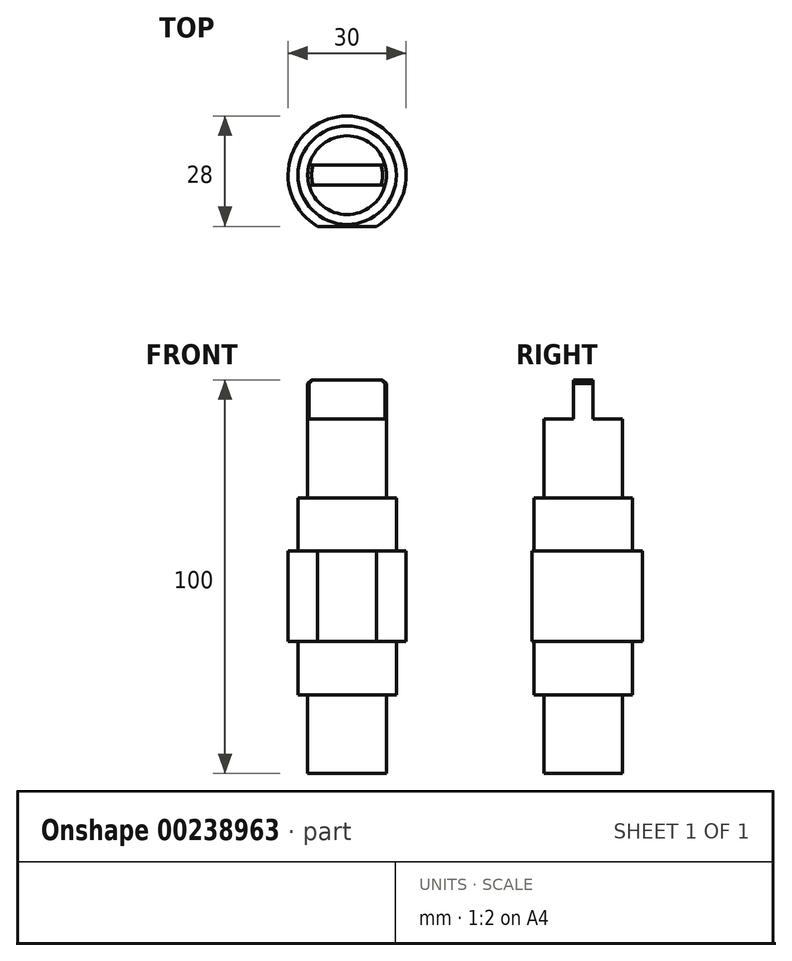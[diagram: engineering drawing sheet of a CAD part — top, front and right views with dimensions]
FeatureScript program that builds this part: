
annotation { "Feature Type Name" : "Feature", "Feature Type Description" : "" }
export const myFeature = defineFeature(function(context is Context, id is Id, definition is map)
    precondition{}
    {
        {
            var Q0;
            Q0=qCreatedBy(makeId("Front.planeOp"),FACE);
            var sketch = newSketch(context, id + "F0", { "sketchPlane" : qUnion([Q0])});
            skLineSegment(sketch, "E0", {"start": v(-15, 11.5) * mm, "end": v(-15, 0) * mm});
            skLineSegment(sketch, "E1", {"start": v(-10, 45) * mm, "end": v(0, 45) * mm});
            skLineSegment(sketch, "E2.MirrorCS", {"start": v(-15, 0) * mm, "end": v(-15, 11.5) * mm});
            skLineSegment(sketch, "E3", {"start": v(0, 45) * mm, "end": v(0, 0) * mm});
            skLineSegment(sketch, "E4", {"start": v(-15, 11.5) * mm, "end": v(-12.5, 11.5) * mm});
            skLineSegment(sketch, "E5", {"start": v(-12.5, 25) * mm, "end": v(-12.5, 11.5) * mm});
            skLineSegment(sketch, "E6", {"start": v(-12.5, 25) * mm, "end": v(-10, 25) * mm});
            skLineSegment(sketch, "E7", {"start": v(-10, 45) * mm, "end": v(-10, 25) * mm});
            skLineSegment(sketch, "E8", {"start": v(12.24, 0) * mm, "end": v(-26.8, 0) * mm, "construction": true});
            skLineSegment(sketch, "E9.MirrorCS", {"start": v(0, -45) * mm, "end": v(0, 0) * mm});
            skLineSegment(sketch, "E10.MirrorCS", {"start": v(-10, -45) * mm, "end": v(0, -45) * mm});
            skLineSegment(sketch, "E11.MirrorCS", {"start": v(-10, -45) * mm, "end": v(-10, -25) * mm});
            skLineSegment(sketch, "E12.MirrorCS", {"start": v(-12.5, -25) * mm, "end": v(-10, -25) * mm});
            skLineSegment(sketch, "E13.MirrorCS", {"start": v(-12.5, -25) * mm, "end": v(-12.5, -11.5) * mm});
            skLineSegment(sketch, "E14.MirrorCS", {"start": v(-15, -11.5) * mm, "end": v(-12.5, -11.5) * mm});
            skLineSegment(sketch, "E15.MirrorCS", {"start": v(-15, 0) * mm, "end": v(-15, -11.5) * mm});
            skSolve(sketch);
        }
        {
            var Q0;
            Q0=qSketchRegion(id+"F0",true);
            var Q1;
            Q1=sQuery(id+"F0.wireOp",EDGE,"E3");
            revolve(context, id + "F1", {"entities" : qUnion([Q0]), "axis" : qUnion([Q1]), "revolveType" : RevolveType.FULL});
        }
        {
            var Q0;
            Q0=qCreatedBy(makeId("Top.planeOp"),FACE);
            var sketch = newSketch(context, id + "F2", { "sketchPlane" : qUnion([Q0])});
            skLineSegment(sketch, "E16", {"start": v(-18, -12.5) * mm, "end": v(24.59, -12.5) * mm, "construction": true});
            skLineSegment(sketch, "E17", {"start": v(-15, -13) * mm, "end": v(0, -13) * mm});
            skLineSegment(sketch, "E18", {"start": v(-15, -17) * mm, "end": v(0, -17) * mm});
            skLineSegment(sketch, "E19.trimOffspring", {"start": v(-15, -13) * mm, "end": v(-15, -17) * mm});
            skLineSegment(sketch, "E20.MirrorCS", {"start": v(15, -13) * mm, "end": v(0, -13) * mm});
            skLineSegment(sketch, "E21.MirrorCS", {"start": v(15, -13) * mm, "end": v(15, -17) * mm});
            skLineSegment(sketch, "E22.MirrorCS", {"start": v(15, -17) * mm, "end": v(0, -17) * mm});
            skCircle(sketch, "E23.0", {"center": v(0, 0) * mm, "radius": 10 * mm, "construction": true});
            skCircle(sketch, "E24.0", {"center": v(0, 0) * mm, "radius": 12.5 * mm, "construction": true});
            skSolve(sketch);
        }
        {
            var Q0;
            Q0=qSketchRegion(id+"F2",true);
            extrude(context, id + "F3", {"entities" : qUnion([Q0]), "operationType" : NewBodyOperationType.REMOVE, "depth" : 25 * mm, "hasSecondDirection" : true, "secondDirectionOppositeDirection" : true, "secondDirectionDepth" : 25 * mm});
        }
        {
            var Q0;
            Q0=makeQuery(id+"F1.opRevolve","SWEPT_FACE",FACE,{"disambiguationData":[OSD([sQuery(id+"F0.wireOp",EDGE,"E1")])]});
            cPlane(context, id + "F4", {"entities" : qUnion([Q0]), "cplaneType" : CPlaneType.OFFSET, "offset" : 0 * mm, "width" : 150 * mm, "height" : 150 * mm});
        }
        {
            var Q0;
            Q0=qCreatedBy(id+"F4.planeOp",FACE);
            var sketch = newSketch(context, id + "F5", { "sketchPlane" : qUnion([Q0])});
            skArc(sketch, "E25.0.0", {"start": v(-9.68, 2.5) * mm, "mid": v(-10, 0) * mm, "end": v(-9.68, -2.5) * mm});
            skLineSegment(sketch, "E26", {"start": v(-9.68, 2.5) * mm, "end": v(9.68, 2.5) * mm});
            skLineSegment(sketch, "E27.MirrorCS", {"start": v(-9.68, -2.5) * mm, "end": v(9.68, -2.5) * mm});
            skArc(sketch, "E28.trimOffspring", {"start": v(9.68, -2.5) * mm, "mid": v(10, 0) * mm, "end": v(9.68, 2.5) * mm});
            skSolve(sketch);
        }
        {
            var Q0;
            Q0 = qSketchRegion(id + "F5", true);
            extrude(context, id + "F6", {"entities" : qUnion([Q0]), "operationType" : NewBodyOperationType.ADD, "depth" : 10 * mm, "hasSecondDirection" : true, "secondDirectionOppositeDirection" : true, "secondDirectionDepth" : 10 * mm});
        }
        {
            var Q0;
            Q0=makeQuery(id+"F6.opExtrude","CAP_EDGE",EDGE,{"disambiguationData":[OSD([sQuery(id+"F5.wireOp",EDGE,"E28.trimOffspring")])],"isStart":false});
            var Q1;
            Q1=makeQuery(id+"F6.opExtrude","CAP_EDGE",EDGE,{"disambiguationData":[OSD([sQuery(id+"F5.wireOp",EDGE,"E25.0.0")])],"isStart":false});
            chamfer(context, id + "F7", {"entities" : qUnion([Q0, Q1]), "width" : 1 * mm, "tangentPropagation" : true});
        }
    });
